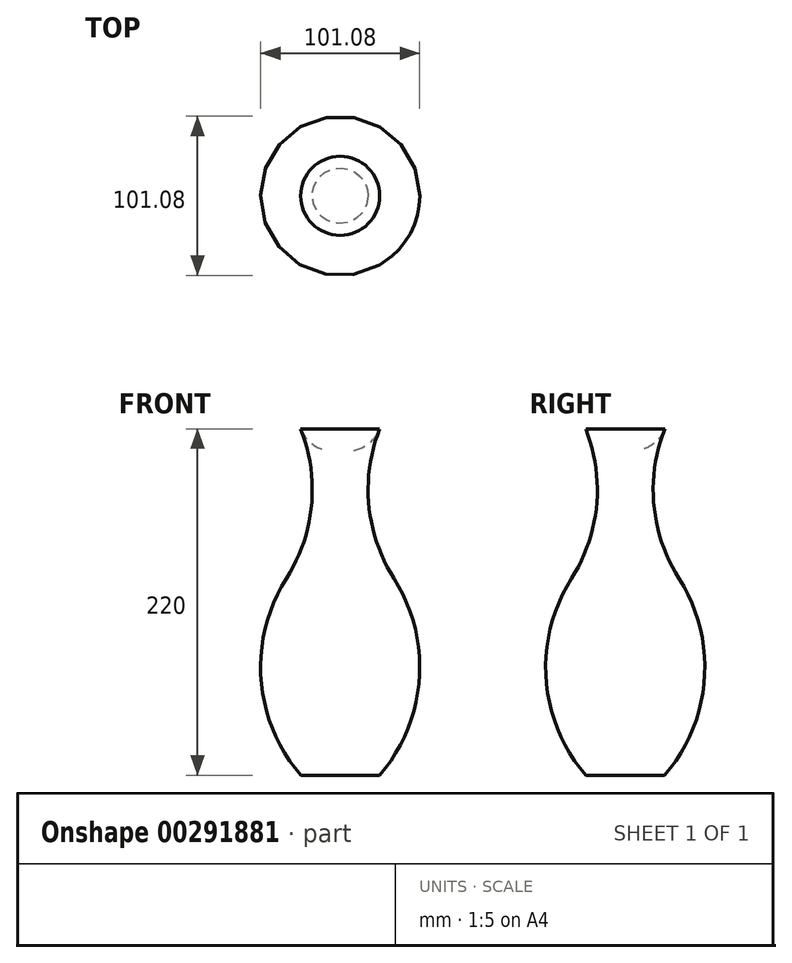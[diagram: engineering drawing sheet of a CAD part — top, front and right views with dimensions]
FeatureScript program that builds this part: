
annotation { "Feature Type Name" : "Feature", "Feature Type Description" : "" }
export const myFeature = defineFeature(function(context is Context, id is Id, definition is map)
    precondition{}
    {
        {
            var Q0;
            Q0=qCreatedBy(makeId("Front.planeOp"),FACE);
            var sketch = newSketch(context, id + "F0", { "sketchPlane" : qUnion([Q0])});
            skLineSegment(sketch, "E0", {"start": v(0, 0) * mm, "end": v(-25, 0) * mm});
            skArc(sketch, "E1", {"start": v(-34.14, 125) * mm, "mid": v(-50.26, 60.99) * mm, "end": v(-25, 0) * mm});
            skArc(sketch, "E2", {"start": v(-34.14, 125) * mm, "mid": v(-18.2, 171.41) * mm, "end": v(-25.1, 220) * mm});
            skArc(sketch, "E3", {"start": v(0, 249.9) * mm, "mid": v(-21.46, 242.43) * mm, "end": v(-25.1, 220) * mm});
            skLineSegment(sketch, "E4", {"start": v(0, 249.9) * mm, "end": v(0, 0) * mm});
            skSolve(sketch);
        }
        {
            var Q0;
            Q0 = qSketchRegion(id + "F0", true);
            var Q1;
            Q1=sQuery(id+"F0.wireOp",EDGE,"E4");
            revolve(context, id + "F1", {"entities" : qUnion([Q0]), "axis" : qUnion([Q1]), "revolveType" : RevolveType.FULL});
        }
    });
